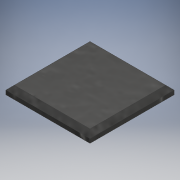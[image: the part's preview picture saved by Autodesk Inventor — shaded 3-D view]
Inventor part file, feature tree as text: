
AUTODESK INVENTOR PART (.ipt)
format: ipt  version: 2019 (Build 230136000, 136)  size: 107,008 bytes
history: native  units: mm
features: chamfer x2, extrude x1, sketch x1
ambient origin geometry x8: Origin, YZ Plane, XZ Plane, XY Plane, X Axis, Y Axis, Z Axis, Center Point
bodies: Solid1 (feature_tree)
feature tree (4):
  extrude  "Extrusion1"  Depth=20.0mm
  chamfer  "Chamfer1"  Distance=2.0mm
  chamfer  "Chamfer2"  Distance=2.0mm Angle=45.0deg
  sketch  "Sketch1"  dims[d0=20.0mm d1=20.0mm d2=2.0mm d3=0.0mm d4=1.0mm d5=2.0mm d6=45.0deg d7=1.0mm d8=2.0mm d9=45.0deg]
